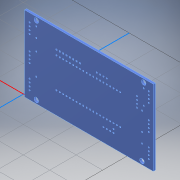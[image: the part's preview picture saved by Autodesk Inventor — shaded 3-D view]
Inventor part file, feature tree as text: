
AUTODESK INVENTOR PART (.ipt)
format: ipt  version: 2022 (Build 260153000, 153)  size: 239,104 bytes
history: native  units: mm
features: other x1, extrude x1, sketch x1
ambient origin geometry x8: Origin, YZ Plane, XZ Plane, XY Plane, X Axis, Y Axis, Z Axis, Center Point
bodies: Body1 (feature_tree)
feature tree (3):
  other  "Твердое тело1"
  extrude  "low_level_contoller_board.brdКонтур"  Depth=1.6mm TaperAngle=0.0deg
  sketch  "Эскиз1"
